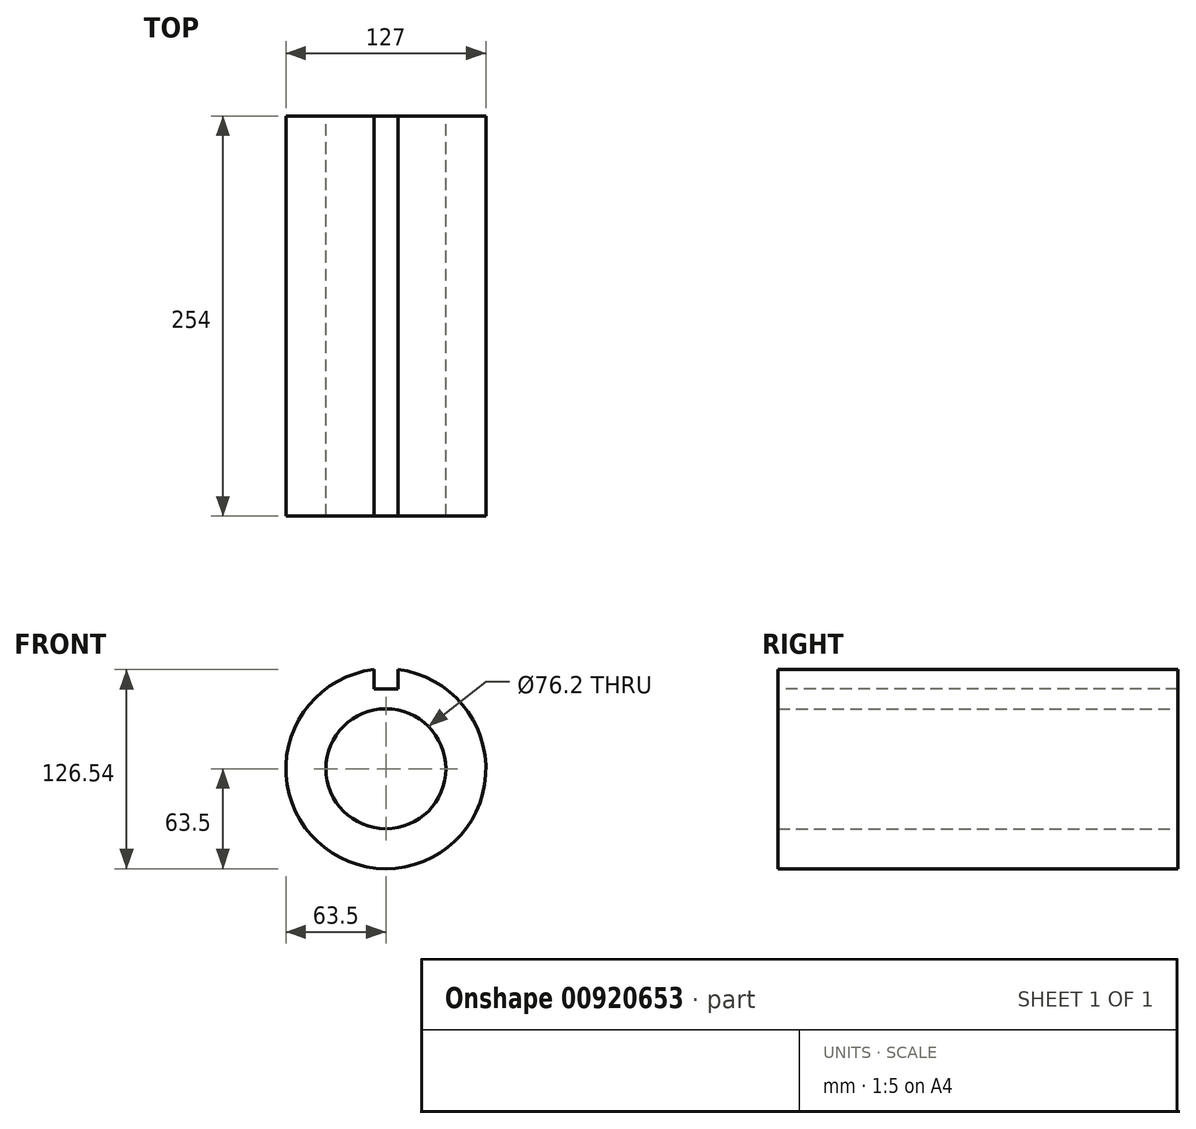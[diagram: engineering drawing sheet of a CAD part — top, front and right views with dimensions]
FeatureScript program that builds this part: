
annotation { "Feature Type Name" : "Feature", "Feature Type Description" : "" }
export const myFeature = defineFeature(function(context is Context, id is Id, definition is map)
    precondition{}
    {
        {
            var Q0;
            Q0=qCreatedBy(makeId("Front.planeOp"),FACE);
            var sketch = newSketch(context, id + "F0", { "sketchPlane" : qUnion([Q0])});
            skCircle(sketch, "E0", {"center": v(0, 0) * mm, "radius": 63.5 * mm});
            skCircle(sketch, "E1", {"center": v(0, 0) * mm, "radius": 38.1 * mm});
            skSolve(sketch);
        }
        {
            var Q0;
            Q0 = qSketchRegion(id + "F0", true);
            extrude(context, id + "F1", {"entities" : qUnion([Q0]), "depth" : 127 * mm, "offsetDistance" : 25.4 * mm, "hasSecondDirection" : true, "secondDirectionOppositeDirection" : true, "secondDirectionDepth" : 127 * mm});
        }
        {
            var Q0;
            Q0=makeQuery(id+"F1.opExtrude","CAP_FACE",FACE,{"disambiguationData":[OSD([sQuery(id+"F0.wireOp",EDGE,"E0"),sQuery(id+"F0.wireOp",EDGE,"E1")])],"isStart":false});
            var sketch = newSketch(context, id + "F2", { "sketchPlane" : qUnion([Q0])});
            skLineSegment(sketch, "E2.bottom", {"start": v(-7.62, 50.8) * mm, "end": v(7.62, 50.8) * mm});
            skLineSegment(sketch, "E2.top", {"start": v(-7.62, 76.2) * mm, "end": v(7.62, 76.2) * mm});
            skLineSegment(sketch, "E2.left", {"start": v(-7.62, 50.8) * mm, "end": v(-7.62, 76.2) * mm});
            skLineSegment(sketch, "E2.right", {"start": v(7.62, 50.8) * mm, "end": v(7.62, 76.2) * mm});
            skPoint(sketch, "E2.middle", {"position": v(0, 63.5) * mm});
            skSolve(sketch);
        }
        {
            var Q0;
            Q0 = qSketchRegion(id + "F2", true);
            extrude(context, id + "F3", {"entities" : qUnion([Q0]), "operationType" : NewBodyOperationType.REMOVE, "endBound" : BoundingType.THROUGH_ALL, "oppositeDirection" : true, "depth" : 25.4 * mm, "offsetDistance" : 25.4 * mm});
        }
    });
